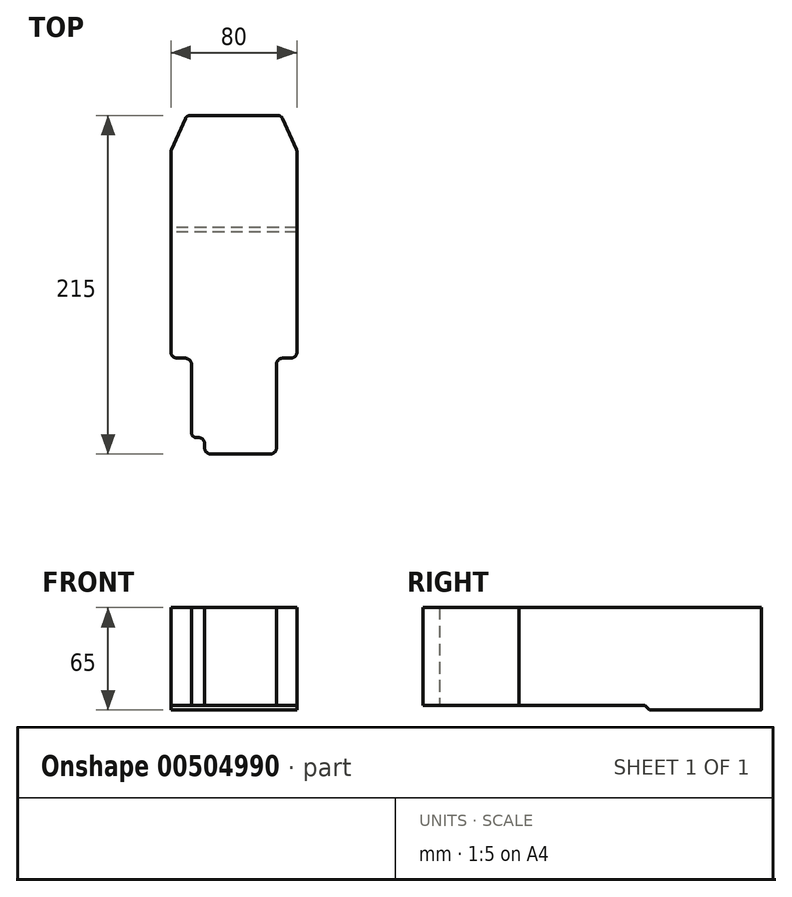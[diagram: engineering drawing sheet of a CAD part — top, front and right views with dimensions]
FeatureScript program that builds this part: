
annotation { "Feature Type Name" : "Feature", "Feature Type Description" : "" }
export const myFeature = defineFeature(function(context is Context, id is Id, definition is map)
    precondition{}
    {
        {
            var Q0;
            Q0=qCreatedBy(makeId("Top.planeOp"),FACE);
            var sketch = newSketch(context, id + "F0", { "sketchPlane" : qUnion([Q0])});
            skLineSegment(sketch, "E0.bottom", {"start": v(-28.06, 43.13) * mm, "end": v(0, 43.13) * mm});
            skLineSegment(sketch, "E0.top", {"start": v(-14.6, -171.87) * mm, "end": v(0, -171.87) * mm});
            skLineSegment(sketch, "E0.left", {"start": v(-40, 20.19) * mm, "end": v(-40, -106.97) * mm});
            skLineSegment(sketch, "E0.right", {"start": v(40, 20.19) * mm, "end": v(40, -106.97) * mm});
            skLineSegment(sketch, "E1.bottom", {"start": v(31, -110.97) * mm, "end": v(36, -110.97) * mm});
            skLineSegment(sketch, "E1.left", {"start": v(27, -114.97) * mm, "end": v(27, -167.87) * mm});
            skLineSegment(sketch, "E2.MirrorCS", {"start": v(-31, -110.97) * mm, "end": v(-36, -110.97) * mm});
            skLineSegment(sketch, "E3.MirrorCS", {"start": v(-27, -114.97) * mm, "end": v(-27, -158.33) * mm});
            skLineSegment(sketch, "E4.bottom", {"start": v(-24, -161.33) * mm, "end": v(-22.6, -161.33) * mm});
            skLineSegment(sketch, "E4.right", {"start": v(-18.6, -165.33) * mm, "end": v(-18.6, -167.87) * mm});
            skPoint(sketch, "E5", {"position": v(-40, -110.97) * mm});
            skPoint(sketch, "E6", {"position": v(40, -110.97) * mm});
            skPoint(sketch, "E7", {"position": v(27, -171.87) * mm});
            skPoint(sketch, "E8", {"position": v(-27, -161.33) * mm});
            skPoint(sketch, "E9", {"position": v(-18.6, -171.87) * mm});
            skPoint(sketch, "E10.orphan", {"position": v(-58.58, -110.97) * mm});
            skPoint(sketch, "E1.right.start.orphan", {"position": v(58.58, -110.97) * mm});
            skPoint(sketch, "E11.orphan", {"position": v(27, -177.8) * mm});
            skPoint(sketch, "E12.trimOffspring.end.orphan", {"position": v(-27, -177.8) * mm});
            skArc(sketch, "E13.filletArc", {"start": v(-18.6, -167.87) * mm, "mid": v(-17.43, -170.7) * mm, "end": v(-14.6, -171.87) * mm});
            skArc(sketch, "E14.filletArc", {"start": v(23, -171.87) * mm, "mid": v(25.83, -170.7) * mm, "end": v(27, -167.87) * mm});
            skArc(sketch, "E15.filletArc", {"start": v(36, -110.97) * mm, "mid": v(38.83, -109.8) * mm, "end": v(40, -106.97) * mm});
            skArc(sketch, "E16.filletArc", {"start": v(-40, -106.97) * mm, "mid": v(-38.83, -109.8) * mm, "end": v(-36, -110.97) * mm});
            skPoint(sketch, "E17.visualSharp", {"position": v(-27, -110.97) * mm});
            skArc(sketch, "E17.filletArc", {"start": v(-27, -114.97) * mm, "mid": v(-28.17, -112.14) * mm, "end": v(-31, -110.97) * mm});
            skPoint(sketch, "E18.visualSharp", {"position": v(27, -110.97) * mm});
            skArc(sketch, "E18.filletArc", {"start": v(31, -110.97) * mm, "mid": v(28.17, -112.14) * mm, "end": v(27, -114.97) * mm});
            skPoint(sketch, "E19.visualSharp", {"position": v(-18.6, -161.33) * mm});
            skArc(sketch, "E19.filletArc", {"start": v(-18.6, -165.33) * mm, "mid": v(-19.77, -162.5) * mm, "end": v(-22.6, -161.33) * mm});
            skLineSegment(sketch, "E20", {"start": v(30.8, 41.36) * mm, "end": v(39.74, 21.41) * mm});
            skLineSegment(sketch, "E21.MirrorCS", {"start": v(-30.8, 41.36) * mm, "end": v(-39.74, 21.41) * mm});
            skPoint(sketch, "E22.orphan", {"position": v(40, 43.13) * mm});
            skPoint(sketch, "E23.visualSharp", {"position": v(-40, 20.83) * mm});
            skArc(sketch, "E23.filletArc", {"start": v(-39.74, 21.41) * mm, "mid": v(-39.93, 20.81) * mm, "end": v(-40, 20.19) * mm});
            skPoint(sketch, "E24.visualSharp", {"position": v(-30, 43.13) * mm});
            skArc(sketch, "E24.filletArc", {"start": v(-28.06, 43.13) * mm, "mid": v(-29.69, 42.65) * mm, "end": v(-30.8, 41.36) * mm});
            skPoint(sketch, "E25.visualSharp", {"position": v(30, 43.13) * mm});
            skArc(sketch, "E25.filletArc", {"start": v(30.8, 41.36) * mm, "mid": v(29.69, 42.65) * mm, "end": v(28.06, 43.13) * mm});
            skPoint(sketch, "E26.visualSharp", {"position": v(40, 20.83) * mm});
            skArc(sketch, "E26.filletArc", {"start": v(40, 20.19) * mm, "mid": v(39.93, 20.81) * mm, "end": v(39.74, 21.41) * mm});
            skArc(sketch, "E27.filletArc", {"start": v(-27, -158.33) * mm, "mid": v(-26.12, -160.46) * mm, "end": v(-24, -161.33) * mm});
            skLineSegment(sketch, "E28", {"start": v(0, 43.13) * mm, "end": v(28.06, 43.13) * mm});
            skLineSegment(sketch, "E29", {"start": v(0, 74.77) * mm, "end": v(0, -227.88) * mm, "construction": true});
            skLineSegment(sketch, "E30", {"start": v(0, -171.87) * mm, "end": v(23, -171.87) * mm});
            skLineSegment(sketch, "E31.3", {"start": v(-37, 20.19) * mm, "end": v(-37, 20.19) * mm});
            skPoint(sketch, "E32.visualSharp", {"position": v(37, -107.97) * mm});
            skSolve(sketch);
        }
        {
            var Q0;
            Q0 = qSketchRegion(id + "F0", true);
            extrude(context, id + "F1", {"entities" : qUnion([Q0]), "depth" : 65 * mm});
        }
        {
            var Q0;
            Q0=makeQuery(id+"F1.opExtrude","SWEPT_FACE",FACE,{"disambiguationData":[OSD([sQuery(id+"F0.wireOp",EDGE,"E0.left")])]});
            var sketch = newSketch(context, id + "F2", { "sketchPlane" : qUnion([Q0])});
            skLineSegment(sketch, "E33.bottom", {"start": v(30.87, 3) * mm, "end": v(180.76, 3) * mm});
            skLineSegment(sketch, "E33.left", {"start": v(30.87, 3) * mm, "end": v(30.87, 0) * mm});
            skLineSegment(sketch, "E33.right", {"start": v(180.76, 3) * mm, "end": v(180.76, 0) * mm});
            skLineSegment(sketch, "E34", {"start": v(30.87, 3) * mm, "end": v(27.87, 0) * mm});
            skLineSegment(sketch, "E35", {"start": v(27.87, 0) * mm, "end": v(30.87, 0) * mm});
            skLineSegment(sketch, "E36", {"start": v(27.87, 0) * mm, "end": v(180.76, 0) * mm});
            skPoint(sketch, "E36.endSnap0", {"position": v(180.76, -1.66) * mm});
            skPoint(sketch, "E37.orphan", {"position": v(180.76, -6.33) * mm});
            skSolve(sketch);
        }
        {
            var Q0;
            {var subQ0=sQuery(id+"F2.wireOp",EDGE,"E33.left");var subQ1=sQuery(id+"F2.wireOp",EDGE,"E33.bottom");var subQ2=makeQuery(id+"F2.imprint","INTERSECT",VERTEX,{"derivedFrom":[subQ1,subQ0,sQuery(id+"F2.wireOp",EDGE,"E34")]});Q0=makeQuery(id+"F2.imprint","IMPRINT",FACE,{"disambiguationData":[TD([[makeQuery(id+"F2.imprint","IMPRINT",EDGE,{"disambiguationData":[TD([[subQ2,-1.0]])],"derivedFrom":subQ1}),-1.0]])]});}
            var Q1;
            {var subQ0=sQuery(id+"F2.wireOp",EDGE,"E34");Q1=makeQuery(id+"F2.imprint","IMPRINT",FACE,{"disambiguationData":[TD([[makeQuery(id+"F2.imprint","IMPRINT",EDGE,{"derivedFrom":subQ0}),1.0]])]});}
            var Q2;
            {var subQ0=sQuery(id+"F2.wireOp",EDGE,"E33.right");Q2=makeQuery(id+"F2.imprint","IMPRINT",FACE,{"disambiguationData":[TD([[makeQuery(id+"F2.imprint","IMPRINT",EDGE,{"derivedFrom":subQ0}),-1.0]])]});}
            extrude(context, id + "F3", {"entities" : qUnion([Q0, Q1, Q2]), "operationType" : NewBodyOperationType.REMOVE, "endBound" : BoundingType.THROUGH_ALL, "oppositeDirection" : true, "depth" : 25 * mm});
        }
    });
